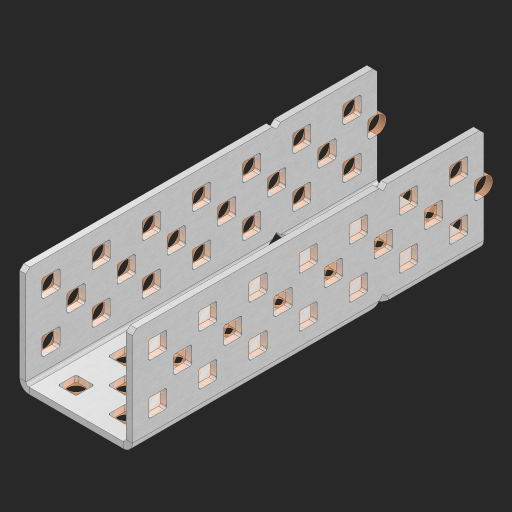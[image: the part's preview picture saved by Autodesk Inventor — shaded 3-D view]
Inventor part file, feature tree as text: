
AUTODESK INVENTOR PART (.ipt)
format: ipt  version: 2023 (Build 270158000, 158)  size: 1,145,344 bytes
history: native  units: in
note: dims shown in document units (in); Inventor stores cm internally (conversion verified against a paired STEP export)
features: other x90, extrude x82, sheet_metal_op x8, sketch x7, mirror x3, pattern_linear x2, chamfer x1
ambient origin geometry x8: Origin, YZ Plane, XZ Plane, XY Plane, X Axis, Y Axis, Z Axis, Center Point
bodies: Solid1 (feature_tree), Body (feature_tree)
feature tree (193):
  sheet_metal_op  "Flanges"
  sheet_metal_op  "Body Pattern"
  pattern_linear  "Center Pattern"  Spacing1=1.0in  [1 undecoded]
  other  "Arc Length"
  mirror  "Notch Mirror"
  pattern_linear  "Notch Pattern"  Spacing1=0.25in  [1 undecoded]
  other  "Diagonal Plane"
  mirror  "Flange 1"
  mirror  "Flange 2"
  chamfer  "End Chamfer"
  sketch  "Sketch1"  dims[d0=1.0in]
  other  "Plate1"
  sketch  "Sketch2"  dims[d1=3.5in]
  other  "Plate2"
  sheet_metal_op  "Bend1"
  sheet_metal_op  "Corner1"
  sketch  "Sketch8"  dims[d2=0.0625in]
  sketch  "Sketch9"  dims[d3=0.0625in]
  other  "Srf91"
  sheet_metal_op  "Body Pattern Sketch"
  other  "Srf92"
  sketch  "Sketch13"  dims[d4=0.0312in]
  sketch  "Sketch15"  dims[d5=0.125in]
  sketch  "Sketch16"  dims[d6=0.0625in d7=1.0in d8=90.0deg d9=0.0312in d10=0.25in d11=0.0625in d12=0.0625in d49=0.182in d50=0.02in d52=0.25in d53=0.0625in d54=0.0in d55=0.172in d56=1.0in d57=0.0in d60=2.7559in d62=0.5in d63=0.7874in d65=0.5in d85=0.1473in d86=0.1782in d88=0.04in d89=0.0625in d90=0.0in d91=0.04in d92=0.0491in d95=2.5in d96=0.04in d97=0.25in d98=45.0deg d99=0.25in d102=2.497in d106=0.182in d107=0.02in d108=0.5in d110=0.0625in d111=0.0in d112=0.172in d113=0.5in d114=0.0in d117=0.5in d118=0.5in d131=0.25in d132=0.25in]
  other  "Srf786"
  other  "Srf889"
  other  "Srf890"
  other  "Srf891"
  other  "Srf892"
  other  "Srf893"
  other  "Srf894"
  other  "Srf1315"
  other  "Srf1316"
  other  "Srf1317"
  other  "Srf1325"
  other  "Srf1326"
  other  "Srf1327"
  other  "Srf1328"
  other  "Srf1329"
  other  "Srf1330"
  other  "Srf1374"
  other  "Srf1375"
  other  "Srf1376"
  other  "Srf1384"
  other  "Srf1385"
  other  "Srf1386"
  other  "Srf1387"
  other  "Srf1388"
  other  "Srf1389"
  other  "Srf1433"
  other  "Srf1434"
  other  "Srf1473"
  other  "Srf1474"
  other  "Srf1475"
  other  "Srf1476"
  other  "Srf1477"
  other  "Srf1478"
  other  "Srf1479"
  other  "Srf1500"
  other  "Srf1501"
  other  "Srf1502"
  other  "Srf1503"
  other  "Srf1504"
  other  "Srf1505"
  other  "Srf1506"
  other  "Srf1507"
  other  "Srf1508"
  other  "Srf1509"
  other  "Srf1510"
  other  "Srf1511"
  other  "Srf1538"
  other  "Srf1539"
  other  "Srf1540"
  other  "Srf1541"
  other  "Srf1542"
  other  "Srf1543"
  other  "Srf1544"
  other  "Srf1545"
  other  "Srf1546"
  other  "Srf1547"
  other  "Srf1548"
  other  "Srf1549"
  other  "Srf1576"
  other  "Srf1577"
  other  "Srf1578"
  other  "Srf1579"
  other  "Srf1580"
  other  "Srf1581"
  other  "Srf1582"
  other  "Srf1583"
  other  "Srf1584"
  other  "Srf1585"
  other  "Srf1586"
  other  "Srf1587"
  other  "Srf1614"
  other  "Srf1615"
  other  "Srf1616"
  other  "Srf1617"
  other  "Srf1618"
  other  "Srf1619"
  other  "Srf1620"
  other  "Srf1621"
  other  "Srf1622"
  other  "Srf1623"
  other  "Srf1624"
  other  "Srf1625"
  sheet_metal_op  "Body Stamp"
  sheet_metal_op  "Body Circle"
  other  "Center Stamp"
  other  "Center Circle"
  sheet_metal_op  "Notch"
  extrude  "ExtrusionSrf92"  Depth=0.0625in
  extrude  "ExtrusionSrf889"  Depth=0.0625in
  extrude  "ExtrusionSrf890"  Depth=0.182in
  extrude  "ExtrusionSrf891"  Depth=0.02in
  extrude  "ExtrusionSrf892"  Depth=0.25in
  extrude  "ExtrusionSrf893"  Depth=0.0625in
  extrude  "ExtrusionSrf894"  TaperAngle=0.0deg  [1 undecoded]
  extrude  "ExtrusionSrf1315"  Depth=0.25in
  extrude  "ExtrusionSrf1316"  Depth=1.0in TaperAngle=0.0deg
  extrude  "ExtrusionSrf1355"  Depth=0.25in
  extrude  "ExtrusionSrf1356"  Depth=0.5in
  extrude  "ExtrusionSrf1357"  Depth=0.25in
  extrude  "ExtrusionSrf1358"  Depth=0.25in
  extrude  "ExtrusionSrf1359"  Depth=0.25in
  extrude  "ExtrusionSrf1360"  Depth=0.0625in
  extrude  "ExtrusionSrf1361"  TaperAngle=0.0deg  [1 undecoded]
  extrude  "ExtrusionSrf1374"  Depth=0.25in
  extrude  "ExtrusionSrf1375"  Depth=0.25in
  extrude  "ExtrusionSrf1414"  Depth=2.5in
  extrude  "ExtrusionSrf1415"  Depth=0.25in TaperAngle=45.0deg
  extrude  "ExtrusionSrf1416"  Depth=0.25in
  extrude  "ExtrusionSrf1417"  Depth=0.25in
  extrude  "ExtrusionSrf1418"  Depth=0.182in
  extrude  "ExtrusionSrf1419"  Depth=0.02in
  extrude  "ExtrusionSrf1420"  Depth=0.5in
  extrude  "ExtrusionSrf1433"  Depth=0.0625in
  extrude  "ExtrusionSrf1434"  TaperAngle=0.0deg  [1 undecoded]
  extrude  "ExtrusionSrf1473"  Depth=0.25in
  extrude  "ExtrusionSrf1474"  Depth=0.5in TaperAngle=0.0deg
  extrude  "ExtrusionSrf1475"  Depth=0.5in
  extrude  "ExtrusionSrf1476"  Depth=0.5in
  extrude  "ExtrusionSrf1477"  Depth=0.25in
  extrude  "ExtrusionSrf1478"  Depth=0.25in
  extrude  "ExtrusionSrf1479"  [1 undecoded]
  extrude  "ExtrusionSrf1500"  [1 undecoded]
  extrude  "ExtrusionSrf1501"  [1 undecoded]
  extrude  "ExtrusionSrf1502"  [1 undecoded]
  extrude  "ExtrusionSrf1503"  [1 undecoded]
  extrude  "ExtrusionSrf1504"  [1 undecoded]
  extrude  "ExtrusionSrf1505"  [1 undecoded]
  extrude  "ExtrusionSrf1506"  [1 undecoded]
  extrude  "ExtrusionSrf1507"  [1 undecoded]
  extrude  "ExtrusionSrf1508"  [1 undecoded]
  extrude  "ExtrusionSrf1509"  [1 undecoded]
  extrude  "ExtrusionSrf1510"  [1 undecoded]
  extrude  "ExtrusionSrf1511"  [1 undecoded]
  extrude  "ExtrusionSrf1538"  [1 undecoded]
  extrude  "ExtrusionSrf1539"  [1 undecoded]
  extrude  "ExtrusionSrf1540"  [1 undecoded]
  extrude  "ExtrusionSrf1541"  [1 undecoded]
  extrude  "ExtrusionSrf1542"  [1 undecoded]
  extrude  "ExtrusionSrf1543"  [1 undecoded]
  extrude  "ExtrusionSrf1544"  [1 undecoded]
  extrude  "ExtrusionSrf1545"  [1 undecoded]
  extrude  "ExtrusionSrf1546"  [1 undecoded]
  extrude  "ExtrusionSrf1547"  [1 undecoded]
  extrude  "ExtrusionSrf1548"  [1 undecoded]
  extrude  "ExtrusionSrf1549"  [1 undecoded]
  extrude  "ExtrusionSrf1576"  [1 undecoded]
  extrude  "ExtrusionSrf1577"  [1 undecoded]
  extrude  "ExtrusionSrf1578"  [1 undecoded]
  extrude  "ExtrusionSrf1579"  [1 undecoded]
  extrude  "ExtrusionSrf1580"  [1 undecoded]
  extrude  "ExtrusionSrf1581"  [1 undecoded]
  extrude  "ExtrusionSrf1582"  [1 undecoded]
  extrude  "ExtrusionSrf1583"  [1 undecoded]
  extrude  "ExtrusionSrf1584"  [1 undecoded]
  extrude  "ExtrusionSrf1585"  [1 undecoded]
  extrude  "ExtrusionSrf1586"  [1 undecoded]
  extrude  "ExtrusionSrf1587"  [1 undecoded]
  extrude  "ExtrusionSrf1614"  [1 undecoded]
  extrude  "ExtrusionSrf1615"  [1 undecoded]
  extrude  "ExtrusionSrf1616"  [1 undecoded]
  extrude  "ExtrusionSrf1617"  [1 undecoded]
  extrude  "ExtrusionSrf1618"  [1 undecoded]
  extrude  "ExtrusionSrf1619"  [1 undecoded]
  extrude  "ExtrusionSrf1620"  [1 undecoded]
  extrude  "ExtrusionSrf1621"  [1 undecoded]
  extrude  "ExtrusionSrf1622"  [1 undecoded]
  extrude  "ExtrusionSrf1623"  [1 undecoded]
  extrude  "ExtrusionSrf1624"  [1 undecoded]
  extrude  "ExtrusionSrf1625"  [1 undecoded]
note: 54 required parameter values undecoded (feature->parameter linkage not recoverable at this tier; creation-order binding heuristic only, values carry confidence <= 0.55)
